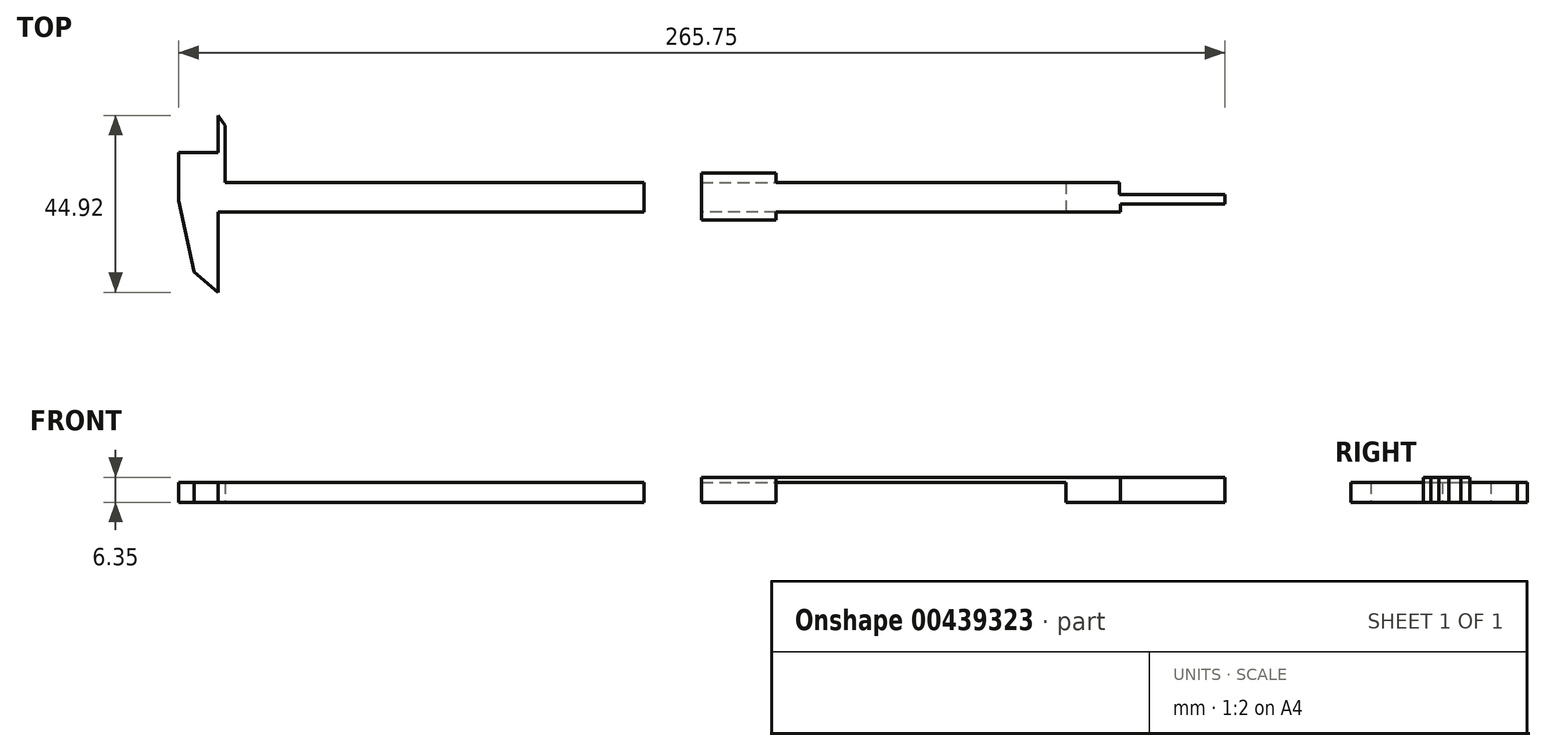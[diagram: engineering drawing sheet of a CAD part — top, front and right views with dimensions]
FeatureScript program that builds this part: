
annotation { "Feature Type Name" : "Feature", "Feature Type Description" : "" }
export const myFeature = defineFeature(function(context is Context, id is Id, definition is map)
    precondition{}
    {
        {
            var Q0;
            Q0=qCreatedBy(makeId("Top.planeOp"),FACE);
            var sketch = newSketch(context, id + "F0", { "sketchPlane" : qUnion([Q0])});
            skLineSegment(sketch, "E0", {"start": v(-55.75, 18.1) * mm, "end": v(50.74, 18.1) * mm});
            skLineSegment(sketch, "E1", {"start": v(50.74, 18.1) * mm, "end": v(50.74, 10.5) * mm});
            skLineSegment(sketch, "E2", {"start": v(50.74, 10.5) * mm, "end": v(-57.53, 10.5) * mm});
            skLineSegment(sketch, "E3", {"start": v(-57.53, 10.5) * mm, "end": v(-57.53, -9.86) * mm});
            skLineSegment(sketch, "E4", {"start": v(-57.53, -9.86) * mm, "end": v(-63.67, -4.69) * mm});
            skLineSegment(sketch, "E5", {"start": v(-63.67, -4.69) * mm, "end": v(-67.54, 13.41) * mm});
            skLineSegment(sketch, "E6", {"start": v(-67.54, 13.41) * mm, "end": v(-67.54, 25.7) * mm});
            skLineSegment(sketch, "E7", {"start": v(-67.54, 25.7) * mm, "end": v(-57.53, 25.7) * mm});
            skLineSegment(sketch, "E8", {"start": v(-57.53, 25.7) * mm, "end": v(-57.53, 35.06) * mm});
            skLineSegment(sketch, "E9", {"start": v(-57.53, 35.06) * mm, "end": v(-55.75, 32.48) * mm});
            skLineSegment(sketch, "E10", {"start": v(-55.75, 32.48) * mm, "end": v(-55.75, 18.1) * mm});
            skLineSegment(sketch, "E11", {"start": v(-41.96, 18.1) * mm, "end": v(-41.96, 20.43) * mm});
            skLineSegment(sketch, "E12", {"start": v(-41.96, 20.43) * mm, "end": v(-22.93, 20.43) * mm});
            skLineSegment(sketch, "E13", {"start": v(-22.93, 20.43) * mm, "end": v(-22.93, 18.1) * mm});
            skLineSegment(sketch, "E14", {"start": v(-22.93, 18.1) * mm, "end": v(64.3, 18.1) * mm});
            skLineSegment(sketch, "E15", {"start": v(64.3, 18.1) * mm, "end": v(64.3, 15.05) * mm});
            skLineSegment(sketch, "E16", {"start": v(64.3, 15.05) * mm, "end": v(91.02, 15.05) * mm});
            skLineSegment(sketch, "E17", {"start": v(91.02, 15.05) * mm, "end": v(91.02, 12.55) * mm});
            skLineSegment(sketch, "E18", {"start": v(91.02, 12.55) * mm, "end": v(64.5, 12.55) * mm});
            skLineSegment(sketch, "E19", {"start": v(64.5, 12.55) * mm, "end": v(64.5, 10.5) * mm});
            skLineSegment(sketch, "E20", {"start": v(64.5, 10.5) * mm, "end": v(-22.93, 10.5) * mm});
            skLineSegment(sketch, "E21", {"start": v(-22.93, 10.5) * mm, "end": v(-22.93, 8.55) * mm});
            skPoint(sketch, "E21.endSnap0", {"position": v(-22.93, 19.26) * mm});
            skLineSegment(sketch, "E22", {"start": v(-22.93, 8.55) * mm, "end": v(-41.96, 8.55) * mm});
            skLineSegment(sketch, "E23", {"start": v(-41.96, 8.55) * mm, "end": v(-41.96, 18.1) * mm});
            skSolve(sketch);
        }
        {
            var Q0;
            {var subQ5=sQuery(id+"F0.wireOp",EDGE,"E1");Q0=makeQuery(id+"F0.imprint","IMPRINT",FACE,{"disambiguationData":[TD([[makeQuery(id+"F0.imprint","IMPRINT",EDGE,{"derivedFrom":subQ5}),-1.0]])]});}
            var Q1;
            {var subQ4=sQuery(id+"F0.wireOp",EDGE,"E3");Q1=makeQuery(id+"F0.imprint","IMPRINT",FACE,{"disambiguationData":[TD([[makeQuery(id+"F0.imprint","IMPRINT",EDGE,{"derivedFrom":subQ4}),-1.0]])]});}
            extrude(context, id + "F1", {"entities" : qUnion([Q0, Q1]), "depth" : 5.08 * mm});
        }
        {
            var Q0;
            {var subQ2=sQuery(id+"F0.wireOp",EDGE,"E11");Q0=makeQuery(id+"F0.imprint","IMPRINT",FACE,{"disambiguationData":[TD([[makeQuery(id+"F0.imprint","IMPRINT",EDGE,{"derivedFrom":subQ2}),-1.0]])]});}
            var Q1;
            {var subQ5=sQuery(id+"F0.wireOp",EDGE,"E1");Q1=makeQuery(id+"F0.imprint","IMPRINT",FACE,{"disambiguationData":[TD([[makeQuery(id+"F0.imprint","IMPRINT",EDGE,{"derivedFrom":subQ5}),-1.0]])]});}
            var Q2;
            {var subQ0=sQuery(id+"F0.wireOp",EDGE,"E21");Q2=makeQuery(id+"F0.imprint","IMPRINT",FACE,{"disambiguationData":[TD([[makeQuery(id+"F0.imprint","IMPRINT",EDGE,{"derivedFrom":subQ0}),-1.0]])]});}
            var Q3;
            {var subQ2=sQuery(id+"F0.wireOp",EDGE,"E1");Q3=makeQuery(id+"F0.imprint","IMPRINT",FACE,{"disambiguationData":[TD([[makeQuery(id+"F0.imprint","IMPRINT",EDGE,{"derivedFrom":subQ2}),1.0]])]});}
            extrude(context, id + "F2", {"entities" : qUnion([Q0, Q1, Q2, Q3]), "depth" : 6.35 * mm});
        }
        {
            var Q0;
            Q0=makeQuery(id+"F1.opExtrude","SWEPT_BODY",BODY,{"disambiguationData":[OSD([sQuery(id+"F0.wireOp",EDGE,"E0"),sQuery(id+"F0.wireOp",EDGE,"E1"),sQuery(id+"F0.wireOp",EDGE,"E2"),sQuery(id+"F0.wireOp",EDGE,"E3"),sQuery(id+"F0.wireOp",EDGE,"E4"),sQuery(id+"F0.wireOp",EDGE,"E5"),sQuery(id+"F0.wireOp",EDGE,"E6"),sQuery(id+"F0.wireOp",EDGE,"E7"),sQuery(id+"F0.wireOp",EDGE,"E8"),sQuery(id+"F0.wireOp",EDGE,"E9"),sQuery(id+"F0.wireOp",EDGE,"E10"),sQuery(id+"F0.wireOp",EDGE,"E14"),sQuery(id+"F0.wireOp",EDGE,"E20")])]});
            var Q1;
            Q1=makeQuery(id+"F2.opExtrude","SWEPT_BODY",BODY,{"disambiguationData":[OSD([sQuery(id+"F0.wireOp",EDGE,"E11"),sQuery(id+"F0.wireOp",EDGE,"E12"),sQuery(id+"F0.wireOp",EDGE,"E13"),sQuery(id+"F0.wireOp",EDGE,"E14"),sQuery(id+"F0.wireOp",EDGE,"E15"),sQuery(id+"F0.wireOp",EDGE,"E16"),sQuery(id+"F0.wireOp",EDGE,"E17"),sQuery(id+"F0.wireOp",EDGE,"E18"),sQuery(id+"F0.wireOp",EDGE,"E19"),sQuery(id+"F0.wireOp",EDGE,"E20"),sQuery(id+"F0.wireOp",EDGE,"E21"),sQuery(id+"F0.wireOp",EDGE,"E22"),sQuery(id+"F0.wireOp",EDGE,"E23")])]});
            booleanBodies(context, id + "F3", {"operationType" : BooleanOperationType.SUBTRACTION, "tools" : qUnion([Q0]), "targets" : qUnion([Q1]), "keepTools" : true});
        }
        {
            var Q0;
            Q0=makeQuery(id+"F2.opExtrude","SWEPT_BODY",BODY,{"disambiguationData":[OSD([sQuery(id+"F0.wireOp",EDGE,"E11"),sQuery(id+"F0.wireOp",EDGE,"E12"),sQuery(id+"F0.wireOp",EDGE,"E13"),sQuery(id+"F0.wireOp",EDGE,"E14"),sQuery(id+"F0.wireOp",EDGE,"E15"),sQuery(id+"F0.wireOp",EDGE,"E16"),sQuery(id+"F0.wireOp",EDGE,"E17"),sQuery(id+"F0.wireOp",EDGE,"E18"),sQuery(id+"F0.wireOp",EDGE,"E19"),sQuery(id+"F0.wireOp",EDGE,"E20"),sQuery(id+"F0.wireOp",EDGE,"E21"),sQuery(id+"F0.wireOp",EDGE,"E22"),sQuery(id+"F0.wireOp",EDGE,"E23")])]});
            transform(context, id + "F4", {"entities" : qUnion([Q0]), "transformType" : TransformType.TRANSLATION_3D, "dx" : 107.19 * mm, "dy" : 0 * mm, "dz" : 0 * mm, "makeCopy" : false});
        }
    });
